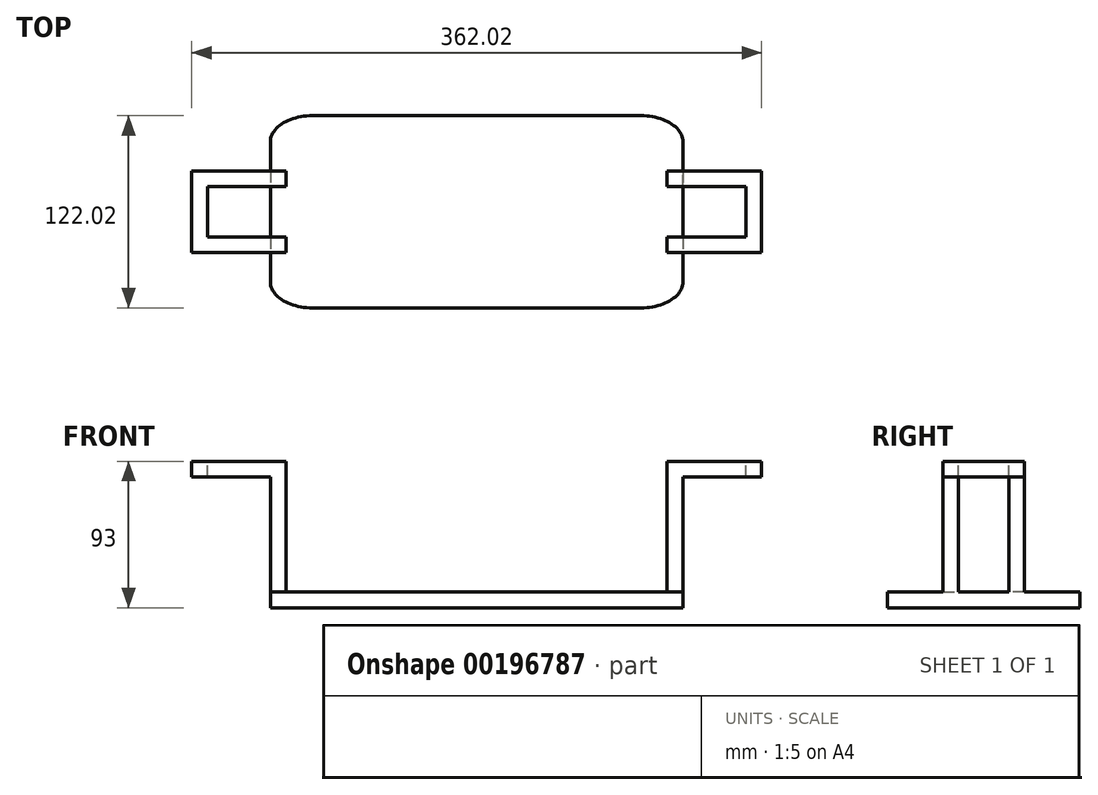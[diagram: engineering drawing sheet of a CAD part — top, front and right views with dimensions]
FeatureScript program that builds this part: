
annotation { "Feature Type Name" : "Feature", "Feature Type Description" : "" }
export const myFeature = defineFeature(function(context is Context, id is Id, definition is map)
    precondition{}
    {
        {
            var Q0;
            Q0=qCreatedBy(makeId("Top.planeOp"),FACE);
            var sketch = newSketch(context, id + "F0", { "sketchPlane" : qUnion([Q0])});
            skLineSegment(sketch, "E0.bottom", {"start": v(-89.26, 68.69) * mm, "end": v(119.53, 68.69) * mm});
            skLineSegment(sketch, "E0.top", {"start": v(-89.26, -53.33) * mm, "end": v(119.53, -53.33) * mm});
            skLineSegment(sketch, "E0.left", {"start": v(-115.87, 52.14) * mm, "end": v(-115.87, -36.78) * mm});
            skLineSegment(sketch, "E0.right", {"start": v(146.15, 52.14) * mm, "end": v(146.15, -36.78) * mm});
            skEllipticalArc(sketch, "E1", {});
            skEllipticalArc(sketch, "E2.MirrorCS", {});
            skPoint(sketch, "E3.endSnap0", {"position": v(-113.86, 7.68) * mm});
            skEllipticalArc(sketch, "E4.MirrorCS", {});
            skEllipticalArc(sketch, "E5.MirrorCS", {});
            skFitSpline(sketch, "E6.0", {"points": [v(-105.87, 52.2) * mm, v(-105.87, 52.16) * mm, v(-105.87, 52.11) * mm, v(-105.85, 52) * mm, v(-105.76, 51.78) * mm, v(-105.56, 51.41) * mm, v(-105.2, 50.93) * mm, v(-104.63, 50.34) * mm, v(-103.86, 49.7) * mm, v(-102.86, 49) * mm, v(-101.65, 48.33) * mm, v(-100.27, 47.7) * mm, v(-98.72, 47.12) * mm, v(-97.04, 46.63) * mm, v(-95.24, 46.24) * mm, v(-93.35, 45.95) * mm, v(-91.72, 45.8) * mm, v(-90.4, 45.74) * mm, v(-89.39, 45.73) * mm, v(-88.38, 45.75) * mm, v(-87.05, 45.82) * mm, v(-85.42, 45.98) * mm, v(-83.54, 46.28) * mm, v(-81.74, 46.69) * mm, v(-80.06, 47.19) * mm, v(-78.52, 47.77) * mm, v(-77.14, 48.41) * mm, v(-75.93, 49.1) * mm, v(-74.94, 49.79) * mm, v(-74.17, 50.45) * mm, v(-73.62, 51.03) * mm, v(-73.25, 51.52) * mm, v(-73.05, 51.89) * mm, v(-72.97, 52.12) * mm, v(-72.95, 52.23) * mm, v(-72.94, 52.27) * mm, v(-72.95, 52.31) * mm, v(-72.97, 52.42) * mm, v(-73.06, 52.65) * mm, v(-73.26, 53.01) * mm, v(-73.63, 53.5) * mm, v(-74.19, 54.08) * mm, v(-74.96, 54.73) * mm, v(-75.96, 55.42) * mm, v(-77.16, 56.1) * mm, v(-78.55, 56.73) * mm, v(-80.1, 57.3) * mm, v(-81.78, 57.8) * mm, v(-83.58, 58.19) * mm, v(-85.47, 58.48) * mm, v(-87.1, 58.62) * mm, v(-88.43, 58.68) * mm, v(-89.43, 58.7) * mm, v(-90.44, 58.67) * mm, v(-91.76, 58.6) * mm, v(-93.4, 58.45) * mm, v(-95.28, 58.15) * mm, v(-97.08, 57.74) * mm, v(-98.76, 57.24) * mm, v(-100.3, 56.66) * mm, v(-101.68, 56.01) * mm, v(-102.88, 55.33) * mm, v(-103.88, 54.64) * mm, v(-104.64, 53.98) * mm, v(-105.2, 53.4) * mm, v(-105.56, 52.9) * mm, v(-105.76, 52.54) * mm, v(-105.85, 52.3) * mm, v(-105.87, 52.2) * mm, v(-105.87, 52.16) * mm, v(-105.87, 52.11) * mm]});
            skLineSegment(sketch, "E6.1", {"start": v(-89.37, 58.69) * mm, "end": v(119.65, 58.69) * mm});
            skLineSegment(sketch, "E6.2", {"start": v(-105.87, 52.16) * mm, "end": v(-105.87, -36.8) * mm});
            skFitSpline(sketch, "E6.3", {"points": [v(136.15, 52.11) * mm, v(136.15, 52.16) * mm, v(136.15, 52.2) * mm, v(136.13, 52.3) * mm, v(136.04, 52.54) * mm, v(135.84, 52.9) * mm, v(135.48, 53.4) * mm, v(134.92, 53.98) * mm, v(134.15, 54.64) * mm, v(133.16, 55.33) * mm, v(131.96, 56.01) * mm, v(130.58, 56.66) * mm, v(129.04, 57.24) * mm, v(127.36, 57.74) * mm, v(125.56, 58.15) * mm, v(123.67, 58.45) * mm, v(122.04, 58.6) * mm, v(120.71, 58.67) * mm, v(119.7, 58.7) * mm, v(118.7, 58.68) * mm, v(117.38, 58.62) * mm, v(115.74, 58.48) * mm, v(113.85, 58.19) * mm, v(112.06, 57.8) * mm, v(110.37, 57.3) * mm, v(108.83, 56.73) * mm, v(107.44, 56.1) * mm, v(106.23, 55.42) * mm, v(105.24, 54.73) * mm, v(104.46, 54.08) * mm, v(103.9, 53.5) * mm, v(103.54, 53.01) * mm, v(103.33, 52.65) * mm, v(103.25, 52.42) * mm, v(103.22, 52.31) * mm, v(103.22, 52.27) * mm, v(103.22, 52.23) * mm, v(103.24, 52.12) * mm, v(103.33, 51.89) * mm, v(103.53, 51.52) * mm, v(103.9, 51.03) * mm, v(104.45, 50.45) * mm, v(105.22, 49.79) * mm, v(106.21, 49.1) * mm, v(107.41, 48.41) * mm, v(108.8, 47.77) * mm, v(110.34, 47.19) * mm, v(112.02, 46.69) * mm, v(113.81, 46.28) * mm, v(115.7, 45.98) * mm, v(117.33, 45.82) * mm, v(118.66, 45.75) * mm, v(119.66, 45.73) * mm, v(120.67, 45.74) * mm, v(122, 45.8) * mm, v(123.63, 45.95) * mm, v(125.52, 46.24) * mm, v(127.32, 46.63) * mm, v(129, 47.12) * mm, v(130.55, 47.7) * mm, v(131.93, 48.33) * mm, v(133.14, 49) * mm, v(134.14, 49.7) * mm, v(134.9, 50.34) * mm, v(135.47, 50.93) * mm, v(135.84, 51.41) * mm, v(136.04, 51.78) * mm, v(136.13, 52) * mm, v(136.15, 52.11) * mm, v(136.15, 52.16) * mm, v(136.15, 52.2) * mm]});
            skFitSpline(sketch, "E6.4", {"points": [v(-105.87, -36.76) * mm, v(-105.87, -36.8) * mm, v(-105.87, -36.84) * mm, v(-105.85, -36.95) * mm, v(-105.76, -37.18) * mm, v(-105.56, -37.54) * mm, v(-105.2, -38.03) * mm, v(-104.64, -38.62) * mm, v(-103.88, -39.28) * mm, v(-102.88, -39.97) * mm, v(-101.68, -40.66) * mm, v(-100.3, -41.3) * mm, v(-98.76, -41.88) * mm, v(-97.08, -42.38) * mm, v(-95.28, -42.8) * mm, v(-93.4, -43.1) * mm, v(-91.76, -43.25) * mm, v(-90.44, -43.32) * mm, v(-89.43, -43.34) * mm, v(-88.43, -43.32) * mm, v(-87.1, -43.27) * mm, v(-85.47, -43.12) * mm, v(-83.58, -42.83) * mm, v(-81.78, -42.44) * mm, v(-80.1, -41.95) * mm, v(-78.55, -41.37) * mm, v(-77.16, -40.74) * mm, v(-75.96, -40.06) * mm, v(-74.96, -39.38) * mm, v(-74.19, -38.73) * mm, v(-73.63, -38.14) * mm, v(-73.26, -37.66) * mm, v(-73.06, -37.3) * mm, v(-72.97, -37.06) * mm, v(-72.95, -36.95) * mm, v(-72.94, -36.91) * mm, v(-72.95, -36.87) * mm, v(-72.97, -36.76) * mm, v(-73.05, -36.53) * mm, v(-73.25, -36.17) * mm, v(-73.62, -35.68) * mm, v(-74.17, -35.09) * mm, v(-74.94, -34.43) * mm, v(-75.93, -33.74) * mm, v(-77.14, -33.05) * mm, v(-78.52, -32.41) * mm, v(-80.06, -31.83) * mm, v(-81.74, -31.33) * mm, v(-83.54, -30.92) * mm, v(-85.42, -30.62) * mm, v(-87.05, -30.46) * mm, v(-88.38, -30.4) * mm, v(-89.39, -30.38) * mm, v(-90.4, -30.39) * mm, v(-91.72, -30.44) * mm, v(-93.35, -30.6) * mm, v(-95.24, -30.88) * mm, v(-97.04, -31.28) * mm, v(-98.72, -31.77) * mm, v(-100.27, -32.34) * mm, v(-101.65, -32.97) * mm, v(-102.86, -33.65) * mm, v(-103.86, -34.33) * mm, v(-104.63, -34.98) * mm, v(-105.2, -35.57) * mm, v(-105.56, -36.06) * mm, v(-105.76, -36.42) * mm, v(-105.85, -36.65) * mm, v(-105.87, -36.76) * mm, v(-105.87, -36.8) * mm, v(-105.87, -36.84) * mm]});
            skLineSegment(sketch, "E6.5", {"start": v(-89.37, -43.33) * mm, "end": v(119.65, -43.33) * mm});
            skFitSpline(sketch, "E6.6", {"points": [v(136.15, -36.84) * mm, v(136.15, -36.8) * mm, v(136.15, -36.76) * mm, v(136.13, -36.65) * mm, v(136.04, -36.42) * mm, v(135.84, -36.06) * mm, v(135.47, -35.57) * mm, v(134.9, -34.98) * mm, v(134.14, -34.33) * mm, v(133.14, -33.65) * mm, v(131.93, -32.97) * mm, v(130.55, -32.34) * mm, v(129, -31.77) * mm, v(127.32, -31.28) * mm, v(125.52, -30.88) * mm, v(123.63, -30.6) * mm, v(122, -30.44) * mm, v(120.67, -30.39) * mm, v(119.66, -30.38) * mm, v(118.66, -30.4) * mm, v(117.33, -30.46) * mm, v(115.7, -30.62) * mm, v(113.81, -30.92) * mm, v(112.02, -31.33) * mm, v(110.34, -31.83) * mm, v(108.8, -32.41) * mm, v(107.41, -33.05) * mm, v(106.21, -33.74) * mm, v(105.22, -34.43) * mm, v(104.45, -35.09) * mm, v(103.9, -35.68) * mm, v(103.53, -36.17) * mm, v(103.33, -36.53) * mm, v(103.24, -36.76) * mm, v(103.22, -36.87) * mm, v(103.22, -36.91) * mm, v(103.22, -36.95) * mm, v(103.25, -37.06) * mm, v(103.33, -37.3) * mm, v(103.54, -37.66) * mm, v(103.9, -38.14) * mm, v(104.46, -38.73) * mm, v(105.24, -39.38) * mm, v(106.23, -40.06) * mm, v(107.44, -40.74) * mm, v(108.83, -41.37) * mm, v(110.37, -41.95) * mm, v(112.06, -42.44) * mm, v(113.85, -42.83) * mm, v(115.74, -43.12) * mm, v(117.38, -43.27) * mm, v(118.7, -43.32) * mm, v(119.7, -43.34) * mm, v(120.71, -43.32) * mm, v(122.04, -43.25) * mm, v(123.67, -43.1) * mm, v(125.56, -42.8) * mm, v(127.36, -42.38) * mm, v(129.04, -41.88) * mm, v(130.58, -41.3) * mm, v(131.96, -40.66) * mm, v(133.16, -39.97) * mm, v(134.15, -39.28) * mm, v(134.92, -38.62) * mm, v(135.48, -38.03) * mm, v(135.84, -37.54) * mm, v(136.04, -37.18) * mm, v(136.13, -36.95) * mm, v(136.15, -36.84) * mm, v(136.15, -36.8) * mm, v(136.15, -36.76) * mm]});
            skLineSegment(sketch, "E6.7", {"start": v(136.15, 52.16) * mm, "end": v(136.15, -36.8) * mm});
            const initialGuessF0  = {"E1": [-0.08940901306515046, 0.05221266648720711, -0.9999941578258009, -0.0034182326236995766, 0.02646502138694948, 0.016474934129939466, 4.704528648974868, 6.282136431318943], "E2.MirrorCS": [0.11968629879002755, 0.052212666487207196, 0.9999941578258005, -0.003418232623742552, 0.02646502138695023, 0.016474934129939375, 0.001048875860734542, 1.578656658204691], "E4.MirrorCS": [-0.08940901306515198, -0.03685575760853395, -0.9999941578258004, 0.003418232623713721, 0.026465021386947934, 0.01647493412993881, 0.0010488758605176343, 1.578656658204863], "E5.MirrorCS": [0.11968629879002758, -0.03685575760853301, 0.9999941578258004, 0.003418232623714273, 0.02646502138695017, 0.016474934129939736, 4.704528648974898, 6.282136431318844]};
            skSetInitialGuess(sketch, initialGuessF0);
            skSolve(sketch);
        }
        {
            var Q0;
            Q0=makeQuery(id+"F0.imprint","IMPRINT",FACE,{"disambiguationData":[TD([[makeQuery(id+"F0.imprint","IMPRINT",EDGE,{"derivedFrom":sQuery(id+"F0.wireOp",EDGE,"E0.bottom")}),-1.0]])]});
            extrude(context, id + "F1", {"entities" : qUnion([Q0]), "depth" : 10 * mm});
        }
        {
            var Q0;
            Q0=qCreatedBy(makeId("Top.planeOp"),FACE);
            cPlane(context, id + "F2", {"entities" : qUnion([Q0]), "cplaneType" : CPlaneType.OFFSET, "offset" : 93 * mm, "width" : 150 * mm, "height" : 150 * mm});
        }
        {
            var Q0;
            Q0=qCreatedBy(id+"F2.planeOp",FACE);
            var sketch = newSketch(context, id + "F3", { "sketchPlane" : qUnion([Q0])});
            skLineSegment(sketch, "E7", {"start": v(0, 0) * mm, "end": v(-91.87, 0) * mm, "construction": true});
            skLineSegment(sketch, "E8", {"start": v(-91.87, 0) * mm, "end": v(-91.87, 7.68) * mm, "construction": true});
            skLineSegment(sketch, "E9", {"start": v(-91.87, 7.68) * mm, "end": v(-165.87, 7.68) * mm, "construction": true});
            skLineSegment(sketch, "E10", {"start": v(-165.87, 7.68) * mm, "end": v(-165.87, 33.68) * mm});
            skLineSegment(sketch, "E11", {"start": v(-165.87, 7.68) * mm, "end": v(-165.87, -18.32) * mm});
            skLineSegment(sketch, "E12", {"start": v(-165.87, 33.68) * mm, "end": v(-105.87, 33.68) * mm});
            skLineSegment(sketch, "E13", {"start": v(-165.87, -18.32) * mm, "end": v(-105.87, -18.32) * mm});
            skLineSegment(sketch, "E14", {"start": v(-105.87, -18.32) * mm, "end": v(-105.87, 33.68) * mm});
            skLineSegment(sketch, "E15", {"start": v(-155.87, -8.32) * mm, "end": v(-105.87, -8.32) * mm});
            skLineSegment(sketch, "E16", {"start": v(-155.87, 23.68) * mm, "end": v(-105.87, 23.68) * mm});
            skLineSegment(sketch, "E17", {"start": v(-155.87, 23.68) * mm, "end": v(-155.87, -8.32) * mm});
            skSolve(sketch);
        }
        {
            var Q0;
            Q0=makeQuery(id+"F3.imprint","IMPRINT",FACE,{"disambiguationData":[TD([[makeQuery(id+"F3.imprint","IMPRINT",EDGE,{"derivedFrom":sQuery(id+"F3.wireOp",EDGE,"E10")}),-1.0]])]});
            extrude(context, id + "F4", {"entities" : qUnion([Q0]), "operationType" : NewBodyOperationType.ADD, "oppositeDirection" : true, "depth" : 10 * mm});
        }
        {
            var Q0;
            Q0=qCreatedBy(makeId("Right.planeOp"),FACE);
            cPlane(context, id + "F5", {"entities" : qUnion([Q0]), "cplaneType" : CPlaneType.OFFSET, "offset" : 15.14 * mm, "width" : 150 * mm, "height" : 150 * mm});
        }
        {
            var Q0;
            Q0=makeQuery(id+"F4.opExtrude","SWEPT_BODY",BODY,{"disambiguationData":[OSD([sQuery(id+"F3.wireOp",EDGE,"E10"),sQuery(id+"F3.wireOp",EDGE,"E11"),sQuery(id+"F3.wireOp",EDGE,"E12"),sQuery(id+"F3.wireOp",EDGE,"E13"),sQuery(id+"F3.wireOp",EDGE,"E14"),sQuery(id+"F3.wireOp",EDGE,"E15"),sQuery(id+"F3.wireOp",EDGE,"E16"),sQuery(id+"F3.wireOp",EDGE,"E17")])]});
            var Q1;
            Q1=qCreatedBy(id+"F5.planeOp",FACE);
            mirror(context, id + "F6", {"operationType" : NewBodyOperationType.ADD, "entities" : qUnion([Q0]), "mirrorPlane" : qUnion([Q1])});
        }
        {
            var Q0;
            Q0=makeQuery(id+"F1.opExtrude","CAP_FACE",FACE,{"disambiguationData":[OSD([sQuery(id+"F0.wireOp",EDGE,"E0.bottom"),sQuery(id+"F0.wireOp",EDGE,"E0.top"),sQuery(id+"F0.wireOp",EDGE,"E0.left"),sQuery(id+"F0.wireOp",EDGE,"E0.right"),sQuery(id+"F0.wireOp",EDGE,"E1"),sQuery(id+"F0.wireOp",EDGE,"E2.MirrorCS"),sQuery(id+"F0.wireOp",EDGE,"E4.MirrorCS"),sQuery(id+"F0.wireOp",EDGE,"E5.MirrorCS"),sQuery(id+"F0.wireOp",EDGE,"E6.0"),sQuery(id+"F0.wireOp",EDGE,"E6.1"),sQuery(id+"F0.wireOp",EDGE,"E6.2"),sQuery(id+"F0.wireOp",EDGE,"E6.3"),sQuery(id+"F0.wireOp",EDGE,"E6.4"),sQuery(id+"F0.wireOp",EDGE,"E6.5"),sQuery(id+"F0.wireOp",EDGE,"E6.6"),sQuery(id+"F0.wireOp",EDGE,"E6.7")])],"isStart":false});
            var sketch = newSketch(context, id + "F7", { "sketchPlane" : qUnion([Q0])});
            skLineSegment(sketch, "E18", {"start": v(0, 0) * mm, "end": v(-105.87, 0) * mm, "construction": true});
            skLineSegment(sketch, "E19", {"start": v(-105.87, 0) * mm, "end": v(-105.87, -8.32) * mm, "construction": true});
            skLineSegment(sketch, "E20", {"start": v(-105.87, -18.32) * mm, "end": v(-105.87, -8.32) * mm});
            skLineSegment(sketch, "E21", {"start": v(-105.87, -18.32) * mm, "end": v(-115.87, -18.32) * mm});
            skLineSegment(sketch, "E22", {"start": v(-115.87, -8.32) * mm, "end": v(-115.87, -18.32) * mm});
            skLineSegment(sketch, "E23", {"start": v(-115.87, -8.32) * mm, "end": v(-105.87, -8.32) * mm});
            skLineSegment(sketch, "E24", {"start": v(-155.87, 7.68) * mm, "end": v(-93.7, 7.68) * mm, "construction": true});
            skLineSegment(sketch, "E25.MirrorCS", {"start": v(-115.87, 23.68) * mm, "end": v(-115.87, 33.68) * mm});
            skLineSegment(sketch, "E26.MirrorCS", {"start": v(-115.87, 23.68) * mm, "end": v(-105.87, 23.68) * mm});
            skLineSegment(sketch, "E27.MirrorCS", {"start": v(-105.87, 33.68) * mm, "end": v(-115.87, 33.68) * mm});
            skLineSegment(sketch, "E28.MirrorCS", {"start": v(-105.87, 33.68) * mm, "end": v(-105.87, 23.68) * mm});
            skLineSegment(sketch, "E29.MirrorCS", {"start": v(146.15, -8.32) * mm, "end": v(136.15, -8.32) * mm});
            skLineSegment(sketch, "E30.MirrorCS", {"start": v(146.15, -8.32) * mm, "end": v(146.15, -18.32) * mm});
            skLineSegment(sketch, "E31.MirrorCS", {"start": v(136.15, -18.32) * mm, "end": v(146.15, -18.32) * mm});
            skLineSegment(sketch, "E32.MirrorCS", {"start": v(136.15, -18.32) * mm, "end": v(136.15, -8.32) * mm});
            skLineSegment(sketch, "E33.MirrorCS", {"start": v(146.15, 23.68) * mm, "end": v(136.15, 23.68) * mm});
            skLineSegment(sketch, "E34.MirrorCS", {"start": v(136.15, 33.68) * mm, "end": v(136.15, 23.68) * mm});
            skLineSegment(sketch, "E35.MirrorCS", {"start": v(146.15, 23.68) * mm, "end": v(146.15, 33.68) * mm});
            skLineSegment(sketch, "E36.MirrorCS", {"start": v(136.15, 33.68) * mm, "end": v(146.15, 33.68) * mm});
            skSolve(sketch);
        }
        {
            var Q0;
            Q0 = qSketchRegion(id + "F7", true);
            var Q1;
            Q1=makeQuery(id+"F4.opExtrude","CAP_FACE",FACE,{"disambiguationData":[OSD([sQuery(id+"F3.wireOp",EDGE,"E10"),sQuery(id+"F3.wireOp",EDGE,"E11"),sQuery(id+"F3.wireOp",EDGE,"E12"),sQuery(id+"F3.wireOp",EDGE,"E13"),sQuery(id+"F3.wireOp",EDGE,"E14"),sQuery(id+"F3.wireOp",EDGE,"E15"),sQuery(id+"F3.wireOp",EDGE,"E16"),sQuery(id+"F3.wireOp",EDGE,"E17")])],"isStart":false});
            var Q2;
            Q2=makeQuery(id+"F1.opExtrude","SWEPT_BODY",BODY,{"disambiguationData":[OSD([sQuery(id+"F0.wireOp",EDGE,"E0.bottom"),sQuery(id+"F0.wireOp",EDGE,"E0.top"),sQuery(id+"F0.wireOp",EDGE,"E0.left"),sQuery(id+"F0.wireOp",EDGE,"E0.right"),sQuery(id+"F0.wireOp",EDGE,"E1"),sQuery(id+"F0.wireOp",EDGE,"E2.MirrorCS"),sQuery(id+"F0.wireOp",EDGE,"E4.MirrorCS"),sQuery(id+"F0.wireOp",EDGE,"E5.MirrorCS"),sQuery(id+"F0.wireOp",EDGE,"E6.0"),sQuery(id+"F0.wireOp",EDGE,"E6.1"),sQuery(id+"F0.wireOp",EDGE,"E6.2"),sQuery(id+"F0.wireOp",EDGE,"E6.3"),sQuery(id+"F0.wireOp",EDGE,"E6.4"),sQuery(id+"F0.wireOp",EDGE,"E6.5"),sQuery(id+"F0.wireOp",EDGE,"E6.6"),sQuery(id+"F0.wireOp",EDGE,"E6.7")])]});
            extrude(context, id + "F8", {"entities" : qUnion([Q0]), "operationType" : NewBodyOperationType.ADD, "endBound" : BoundingType.UP_TO_SURFACE, "endBoundEntityFace" : qUnion([Q1]), "endBoundEntityBody" : qUnion([Q2]), "depth" : 25 * mm});
        }
    });
